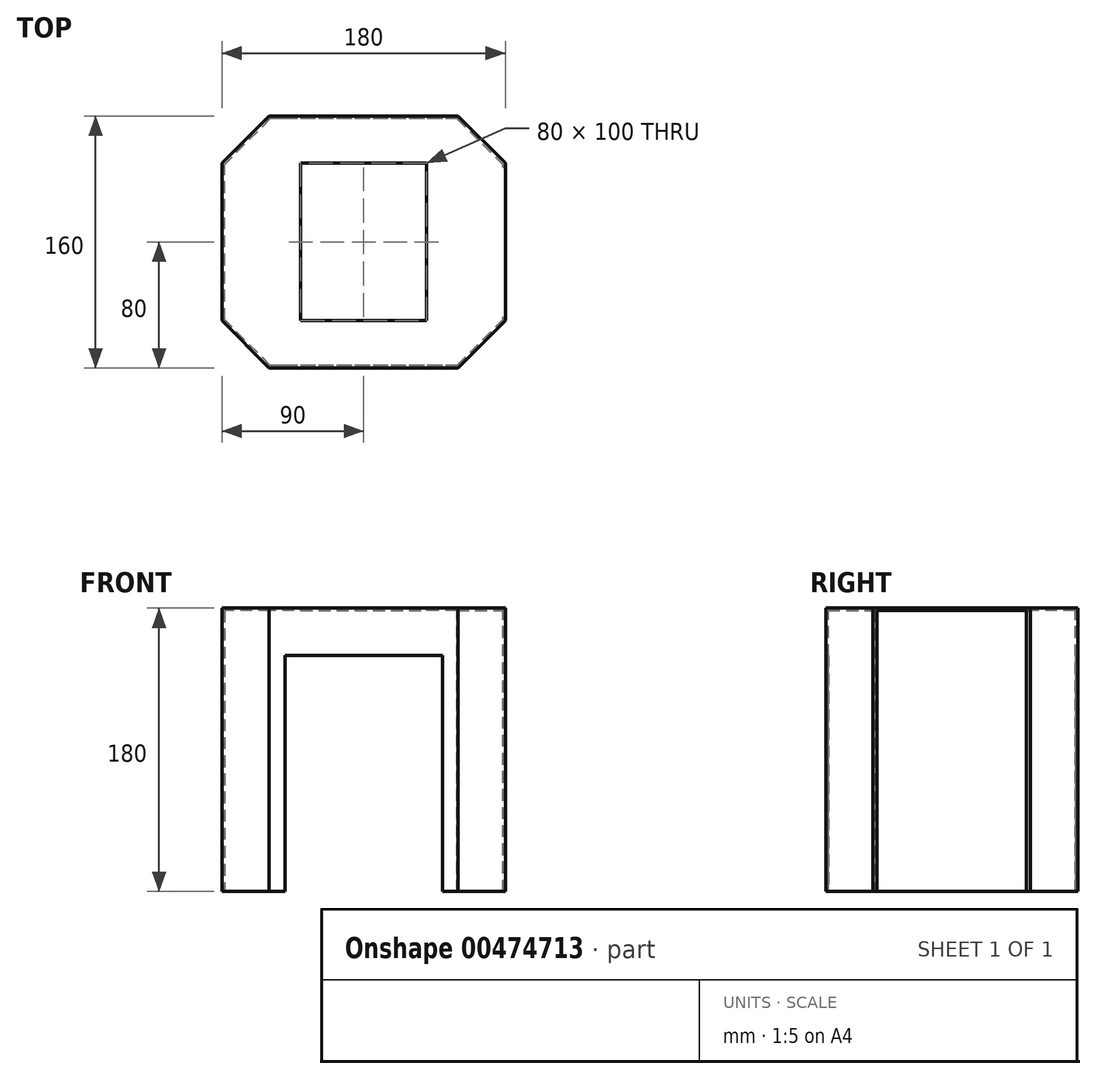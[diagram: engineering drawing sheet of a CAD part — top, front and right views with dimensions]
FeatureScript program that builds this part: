
annotation { "Feature Type Name" : "Feature", "Feature Type Description" : "" }
export const myFeature = defineFeature(function(context is Context, id is Id, definition is map)
    precondition{}
    {
        {
            var Q0;
            Q0=qCreatedBy(makeId("Front.planeOp"),FACE);
            var sketch = newSketch(context, id + "F0", { "sketchPlane" : qUnion([Q0])});
            skLineSegment(sketch, "E0.bottom", {"start": v(90, -90) * mm, "end": v(-90, -90) * mm});
            skLineSegment(sketch, "E0.top", {"start": v(90, 90) * mm, "end": v(-90, 90) * mm});
            skLineSegment(sketch, "E0.left", {"start": v(90, -90) * mm, "end": v(90, 90) * mm});
            skLineSegment(sketch, "E0.right", {"start": v(-90, -90) * mm, "end": v(-90, 90) * mm});
            skPoint(sketch, "E0.middle", {"position": v(0, 0) * mm});
            skLineSegment(sketch, "E1", {"start": v(0, 47.1) * mm, "end": v(0, -52.94) * mm, "construction": true});
            skLineSegment(sketch, "E2", {"start": v(0, -90) * mm, "end": v(0, 60) * mm});
            skLineSegment(sketch, "E3", {"start": v(0, 60) * mm, "end": v(50, 60) * mm});
            skLineSegment(sketch, "E4", {"start": v(50, 60) * mm, "end": v(50, -90) * mm});
            skLineSegment(sketch, "E5", {"start": v(50, -90) * mm, "end": v(0, -90) * mm});
            skLineSegment(sketch, "E6.MirrorCS", {"start": v(0, 60) * mm, "end": v(-50, 60) * mm});
            skLineSegment(sketch, "E7.MirrorCS", {"start": v(-50, 60) * mm, "end": v(-50, -90) * mm});
            skLineSegment(sketch, "E8.MirrorCS", {"start": v(-50, -90) * mm, "end": v(0, -90) * mm});
            skSolve(sketch);
        }
        {
            var Q0;
            Q0=makeQuery(id+"F0.imprint","IMPRINT",FACE,{"disambiguationData":[TD([[makeQuery(id+"F0.imprint","IMPRINT",EDGE,{"derivedFrom":sQuery(id+"F0.wireOp",EDGE,"E0.top")}),1.0]])]});
            extrude(context, id + "F1", {"entities" : qUnion([Q0]), "endBound" : BoundingType.SYMMETRIC, "depth" : 160 * mm});
        }
        {
            var Q0;
            Q0=makeQuery(id+"F1.opExtrude","CAP_EDGE",EDGE,{"disambiguationData":[OSD([sQuery(id+"F0.wireOp",EDGE,"E0.right")])],"isStart":false});
            var Q1;
            Q1=makeQuery(id+"F1.opExtrude","CAP_EDGE",EDGE,{"disambiguationData":[OSD([sQuery(id+"F0.wireOp",EDGE,"E0.left")])],"isStart":false});
            var Q2;
            Q2=makeQuery(id+"F1.opExtrude","CAP_EDGE",EDGE,{"disambiguationData":[OSD([sQuery(id+"F0.wireOp",EDGE,"E0.left")])],"isStart":true});
            var Q3;
            Q3=makeQuery(id+"F1.opExtrude","CAP_EDGE",EDGE,{"disambiguationData":[OSD([sQuery(id+"F0.wireOp",EDGE,"E0.right")])],"isStart":true});
            chamfer(context, id + "F2", {"entities" : qUnion([Q0, Q1, Q2, Q3]), "width" : 30 * mm, "tangentPropagation" : true});
        }
        {
            var Q0;
            {var subQ0=sQuery(id+"F0.wireOp",EDGE,"E0.bottom");Q0=makeQuery(id+"F1.opExtrude","SWEPT_FACE",FACE,{"disambiguationData":[OSD([subQ0]),TDD([makeQuery(id+"F0.imprint","IMPRINT",EDGE,{"disambiguationData":[TD([[makeQuery(id+"F0.imprint","INTERSECT",VERTEX,{"derivedFrom":[subQ0,sQuery(id+"F0.wireOp",EDGE,"E0.left")]}),-1.0]])],"derivedFrom":subQ0})])]});}
            var Q1;
            {var subQ0=sQuery(id+"F0.wireOp",EDGE,"E0.bottom");Q1=makeQuery(id+"F1.opExtrude","SWEPT_FACE",FACE,{"disambiguationData":[OSD([subQ0]),TDD([makeQuery(id+"F0.imprint","IMPRINT",EDGE,{"disambiguationData":[TD([[makeQuery(id+"F0.imprint","INTERSECT",VERTEX,{"derivedFrom":[subQ0,sQuery(id+"F0.wireOp",EDGE,"E0.right")]}),1.0]])],"derivedFrom":subQ0})])]});}
            var Q2;
            Q2=makeQuery(id+"F1.opExtrude","SWEPT_FACE",FACE,{"disambiguationData":[OSD([sQuery(id+"F0.wireOp",EDGE,"E3"),sQuery(id+"F0.wireOp",EDGE,"E6.MirrorCS")])]});
            var Q3;
            Q3=makeQuery(id+"F1.opExtrude","SWEPT_FACE",FACE,{"disambiguationData":[OSD([sQuery(id+"F0.wireOp",EDGE,"E4")])]});
            var Q4;
            Q4=makeQuery(id+"F1.opExtrude","SWEPT_FACE",FACE,{"disambiguationData":[OSD([sQuery(id+"F0.wireOp",EDGE,"E7.MirrorCS")])]});
            shell(context, id + "F3", {"entities" : qUnion([Q0, Q1, Q2, Q3, Q4]), "thickness" : 1.6 * mm});
        }
        {
            var Q0;
            Q0=makeQuery(id+"F1.opExtrude","SWEPT_FACE",FACE,{"disambiguationData":[OSD([sQuery(id+"F0.wireOp",EDGE,"E0.left")])]});
            var sketch = newSketch(context, id + "F4", { "sketchPlane" : qUnion([Q0])});
            skLineSegment(sketch, "E9", {"start": v(0, 53.78) * mm, "end": v(0, -56.51) * mm, "construction": true});
            skPoint(sketch, "E9.startSnap0", {"position": v(0, 90) * mm});
            skPoint(sketch, "E10.0.3.end.orphan", {"position": v(-80, -90) * mm});
            skPoint(sketch, "E10.0.3.start.orphan", {"position": v(-80, 90) * mm});
            skPoint(sketch, "E11.orphan", {"position": v(-50, -90) * mm});
            skPoint(sketch, "E12.0.0.end.orphan", {"position": v(50, -90) * mm});
            skPoint(sketch, "E12.0.1.start.orphan", {"position": v(80, -90) * mm});
            skPoint(sketch, "E12.0.2.end.orphan", {"position": v(80, 90) * mm});
            skPoint(sketch, "E12.0.2.start.orphan", {"position": v(50, 90) * mm});
            skPoint(sketch, "E13.orphan", {"position": v(-50, 90) * mm});
            skPoint(sketch, "E14.MirrorCS.start.orphan", {"position": v(0, -90) * mm});
            skLineSegment(sketch, "E15", {"start": v(50, -90) * mm, "end": v(47.5, -90) * mm});
            skLineSegment(sketch, "E16", {"start": v(47.5, -90) * mm, "end": v(-47.5, -90) * mm});
            skLineSegment(sketch, "E17", {"start": v(-47.5, -90) * mm, "end": v(-47.5, 88.4) * mm});
            skLineSegment(sketch, "E18", {"start": v(0, 90) * mm, "end": v(47.5, 90) * mm});
            skLineSegment(sketch, "E19", {"start": v(47.5, 88.4) * mm, "end": v(47.5, -90) * mm});
            skLineSegment(sketch, "E20.0", {"start": v(-47.5, 88.4) * mm, "end": v(47.5, 88.4) * mm});
            skLineSegment(sketch, "E21.0", {"start": v(-47.5, 28.4) * mm, "end": v(47.5, 28.4) * mm});
            skSolve(sketch);
        }
        {
            var Q0;
            Q0 = qSketchRegion(id + "F4", true);
            extrude(context, id + "F5", {"entities" : qUnion([Q0]), "operationType" : NewBodyOperationType.REMOVE, "oppositeDirection" : true, "depth" : 25 * mm});
        }
        {
            var Q0;
            Q0=makeQuery(id+"F1.opExtrude","SWEPT_FACE",FACE,{"disambiguationData":[OSD([sQuery(id+"F0.wireOp",EDGE,"E0.top")])]});
            var sketch = newSketch(context, id + "F6", { "sketchPlane" : qUnion([Q0])});
            skLineSegment(sketch, "E22.bottom", {"start": v(40, -50) * mm, "end": v(-40, -50) * mm});
            skLineSegment(sketch, "E22.top", {"start": v(40, 50) * mm, "end": v(-40, 50) * mm});
            skLineSegment(sketch, "E22.left", {"start": v(40, -50) * mm, "end": v(40, 50) * mm});
            skLineSegment(sketch, "E22.right", {"start": v(-40, -50) * mm, "end": v(-40, 50) * mm});
            skPoint(sketch, "E22.middle", {"position": v(0, 0) * mm});
            skSolve(sketch);
        }
        {
            var Q0;
            Q0=makeQuery(id+"F6.imprint","IMPRINT",FACE,{"disambiguationData":[TD([[makeQuery(id+"F6.imprint","IMPRINT",EDGE,{"derivedFrom":sQuery(id+"F6.wireOp",EDGE,"E22.bottom")}),-1.0]])]});
            extrude(context, id + "F7", {"entities" : qUnion([Q0]), "operationType" : NewBodyOperationType.REMOVE, "oppositeDirection" : true, "depth" : 25 * mm});
        }
    });
